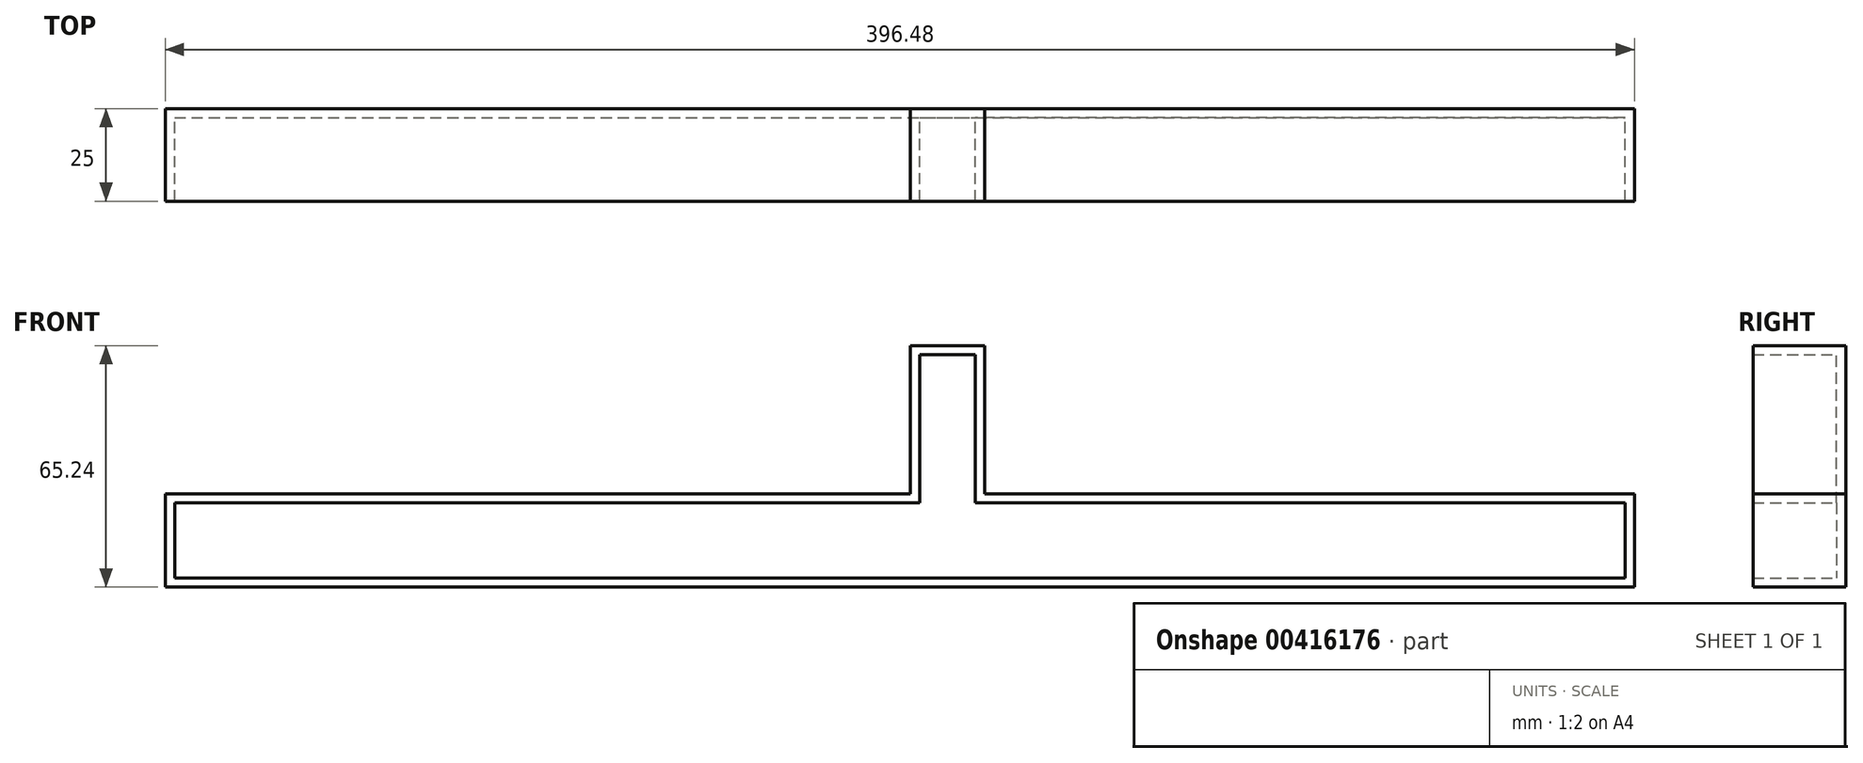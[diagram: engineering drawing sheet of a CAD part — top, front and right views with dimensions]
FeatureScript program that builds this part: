
annotation { "Feature Type Name" : "Feature", "Feature Type Description" : "" }
export const myFeature = defineFeature(function(context is Context, id is Id, definition is map)
    precondition{}
    {
        {
            var Q0;
            Q0=qCreatedBy(makeId("Front.planeOp"),FACE);
            var sketch = newSketch(context, id + "F0", { "sketchPlane" : qUnion([Q0])});
            skLineSegment(sketch, "E0.top", {"start": v(-10, 40) * mm, "end": v(10, 40) * mm});
            skLineSegment(sketch, "E0.left", {"start": v(-10, 0) * mm, "end": v(-10, 40) * mm});
            skLineSegment(sketch, "E0.right", {"start": v(10, 0) * mm, "end": v(10, 40) * mm});
            skLineSegment(sketch, "E1.bottom", {"start": v(-211.1, 0) * mm, "end": v(-10, 0) * mm});
            skLineSegment(sketch, "E1.top", {"start": v(-211.1, -25.24) * mm, "end": v(185.37, -25.24) * mm});
            skLineSegment(sketch, "E1.left", {"start": v(-211.1, 0) * mm, "end": v(-211.1, -25.24) * mm});
            skLineSegment(sketch, "E1.right", {"start": v(185.37, 0) * mm, "end": v(185.37, -25.24) * mm});
            skLineSegment(sketch, "E2", {"start": v(185.37, 0) * mm, "end": v(10, 0) * mm});
            skSolve(sketch);
        }
        {
            var Q0;
            Q0=makeQuery(id+"F0.imprint","IMPRINT",FACE,{"disambiguationData":[TD([[makeQuery(id+"F0.imprint","IMPRINT",EDGE,{"derivedFrom":sQuery(id+"F0.wireOp",EDGE,"E0.top")}),-1.0]])]});
            var Q1;
            Q1=sQuery(id+"F0.wireOp",EDGE,"8f59864f-199c-4b75-923c-b1f7579a69d0.trimOffspring");
            extrude(context, id + "F1", {"entities" : qUnion([Q0]), "surfaceEntities" : qUnion([Q1]), "depth" : 25 * mm});
        }
        {
            var Q0;
            Q0=makeQuery(id+"F1.opExtrude","CAP_FACE",FACE,{"disambiguationData":[OSD([sQuery(id+"F0.wireOp",EDGE,"E0.top"),sQuery(id+"F0.wireOp",EDGE,"E0.left"),sQuery(id+"F0.wireOp",EDGE,"E0.right"),sQuery(id+"F0.wireOp",EDGE,"E1.bottom"),sQuery(id+"F0.wireOp",EDGE,"E1.top"),sQuery(id+"F0.wireOp",EDGE,"E1.left"),sQuery(id+"F0.wireOp",EDGE,"E1.right"),sQuery(id+"F0.wireOp",EDGE,"E2")])],"isStart":false});
            shell(context, id + "F2", {"entities" : qUnion([Q0]), "thickness" : 2.5 * mm});
        }
    });
